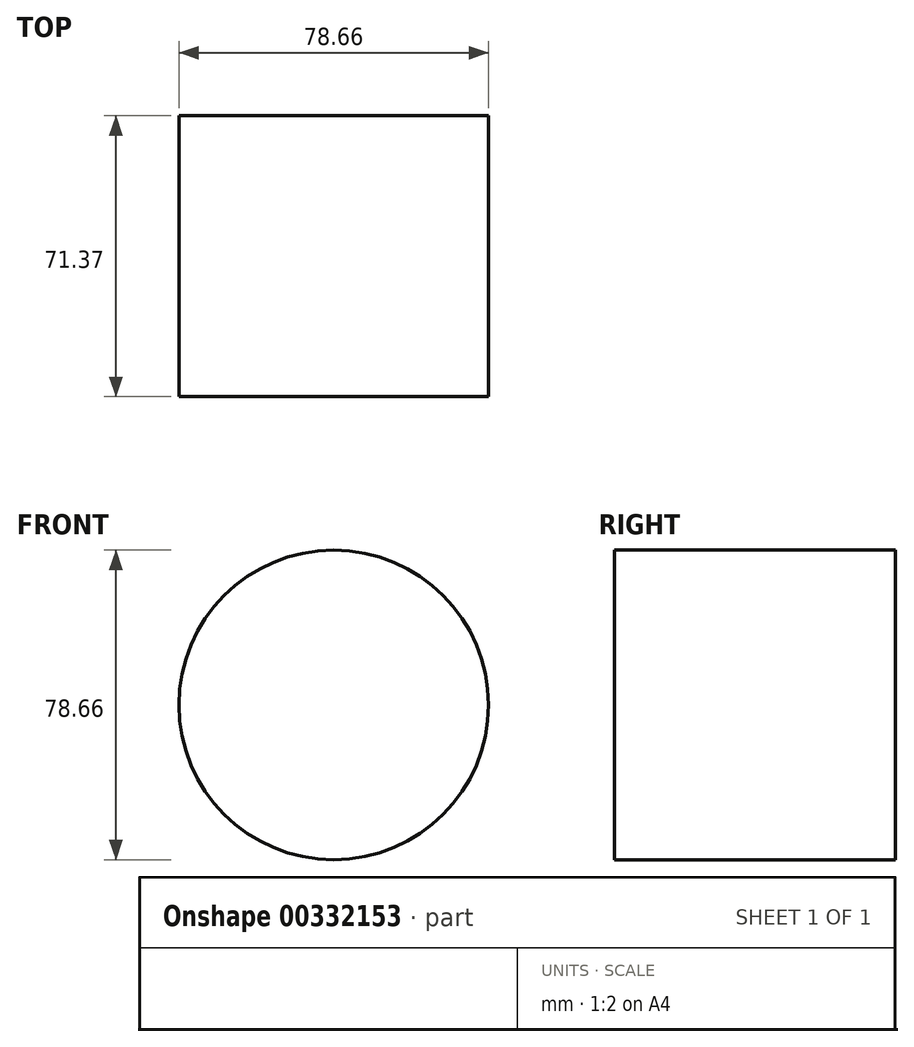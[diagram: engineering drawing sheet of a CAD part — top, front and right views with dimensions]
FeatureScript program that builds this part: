
annotation { "Feature Type Name" : "Feature", "Feature Type Description" : "" }
export const myFeature = defineFeature(function(context is Context, id is Id, definition is map)
    precondition{}
    {
        {
            var Q0;
            Q0=qCreatedBy(makeId("Front.planeOp"),FACE);
            var sketch = newSketch(context, id + "F0", { "sketchPlane" : qUnion([Q0])});
            skCircle(sketch, "E0", {"center": v(0, 0) * mm, "radius": 39.33 * mm});
            skSolve(sketch);
        }
        {
            var Q0;
            Q0=makeQuery(id+"F0.imprint","IMPRINT",FACE,{"disambiguationData":[TD([[makeQuery(id+"F0.imprint","IMPRINT",EDGE,{"derivedFrom":sQuery(id+"F0.wireOp",EDGE,"E0")}),1.0]])]});
            extrude(context, id + "F1", {"entities" : qUnion([Q0]), "depth" : 71.37 * mm});
        }
    });
